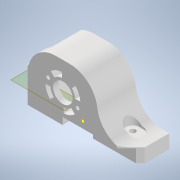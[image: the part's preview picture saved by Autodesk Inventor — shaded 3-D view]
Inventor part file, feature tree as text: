
AUTODESK INVENTOR PART (.ipt)
format: ipt  version: 2020 (Build 240168000, 168)  size: 481,280 bytes
history: native  units: in
note: dims shown in document units (in); Inventor stores cm internally (conversion verified against a paired STEP export)
features: sketch x16, extrude x15, reference x15, fillet x8, other x6, plane x2, chamfer x2, projected_geometry x2
ambient origin geometry x8: Origin, YZ Plane, XZ Plane, XY Plane, X Axis, Y Axis, Z Axis, Center Point
bodies: Solid1 (feature_tree)
feature tree (66):
  extrude  "Extrusion1"  Depth=0.7047in
  extrude  "Extrusion2"  Depth=2.25in
  sketch  "Sketch3"  dims[d4=1.7441in d5=1.7598in d6=2.5in d7=1.25in]
  plane  "Work Plane1"
  extrude  "Extrusion3"  Depth=1.7598in
  fillet  "Fillet1"  Radius=2.5in
  fillet  "Fillet2"  Radius=1.25in
  chamfer  "Chamfer1"  Distance=1.0in
  extrude  "Extrusion4"  Depth=0.8in TaperAngle=0.0deg
  extrude  "Extrusion5"  Depth=1.0in
  extrude  "Extrusion6"  Depth=0.125in TaperAngle=45.0deg
  extrude  "Extrusion7"  Depth=1.875in
  fillet  "Fillet3"  Radius=0.5in
  fillet  "Fillet4"  Radius=0.5in
  fillet  "Fillet5"  Radius=0.203in
  extrude  "Extrusion8"  Depth=0.5in
  extrude  "Extrusion9"  Depth=1.0in TaperAngle=0.0deg
  extrude  "Extrusion11"  Depth=0.1in
  extrude  "Extrusion12"  Depth=1.0in TaperAngle=0.0deg
  extrude  "Extrusion13"  Depth=0.1in
  extrude  "Extrusion14"  TaperAngle=0.0deg  [1 undecoded]
  plane  "Work Plane2"
  sketch  "Sketch15"  dims[d45=0.1in d47=0.0in d48=0.0in]
  extrude  "Extrusion15"  Depth=0.05in
  fillet  "Fillet6"  Radius=0.3in
  chamfer  "Chamfer6"  Distance=2.5in
  extrude  "Extrusion16"  Depth=0.05in
  fillet  "Fillet7"  Radius=1.2299in
  fillet  "Fillet8"  Radius=0.5in
  sketch  "Sketch1"  dims[d0=0.689in d1=0.7047in]
  reference  "Reference1"
  reference  "Reference2"
  reference  "Reference3"
  reference  "Reference4"
  reference  "Reference5"
  sketch  "Sketch2"  dims[d2=2.9in d3=2.25in]
  projected_geometry  "Projected Loop1"
  sketch  "Sketch4"  dims[d8=1.0in d10=1.0in d11=0.0in]
  reference  "Reference6"
  sketch  "Sketch5"  dims[d12=1.7598in d13=0.8in d14=0.0in]
  sketch  "Sketch6"  dims[d15=0.8in d16=0.0in d17=1.0in]
  reference  "Reference7"
  reference  "Reference8"
  reference  "Reference9"
  reference  "Reference10"
  reference  "Reference11"
  reference  "Reference12"
  sketch  "Sketch7"  dims[d18=1.0in d19=0.5in d20=0.125in d21=45.0deg]
  reference  "Reference13"
  reference  "Reference14"
  sketch  "Sketch8"  dims[d26=1.675in d27=1.875in d28=0.5in d29=0.5in d30=0.203in]
  sketch  "Sketch9"  dims[d31=0.0in d32=0.0in d33=0.5in]
  projected_geometry  "Projected Loop2"
  sketch  "Sketch11"  dims[d34=0.5in d35=1.0in d36=0.0in]
  sketch  "Sketch12"  dims[d37=0.0in d38=0.0in d39=0.1in]
  sketch  "Sketch13"  dims[d40=0.1in d41=1.0in d42=0.0in]
  reference  "Reference15"
  sketch  "Sketch14"  dims[d43=0.25in d44=0.1in]
  sketch  "Sketch16"  dims[d49=0.05in d50=0.5in d52=0.3in d53=2.5in d54=0.0in]
  sketch  "Sketch17"  dims[d58=0.5in d59=1.2in d71=1.2299in d72=0.5in d73=1.0in d74=0.0in d75=0.2188in d76=2.5in d77=0.75in d78=0.3438in d79=0.0in d80=0.25in d81=0.5in d82=3.0in d83=0.725in d84=0.2in d85=0.0in d86=0.0in d87=0.5in d88=1.0in d89=0.0in d90=-0.5in d91=0.5in d92=0.5in d93=0.0in d94=0.125in d95=0.05in d96=0.125in d97=45.0deg d98=45.0deg d99=0.6in d100=1.0in d101=0.0in d102=0.125in d103=0.05in]
  other  "<userpath>\Documents\FRC\2020\IntakeShooter\spacers.iam"
  other  "spacers.iam"
  other  "VersaFrame_Side_Bearing_Gusset_217-3553:1"
  other  "775pro_775pro_Connect_and_GT2_Pulley_217-6347:1"
  other  "1x1x18:1"
  other  "VersaFrame_End_Bearing_Gusset_217-3554:1"
note: 1 required parameter value undecoded (feature->parameter linkage not recoverable at this tier; creation-order binding heuristic only, values carry confidence <= 0.55)
